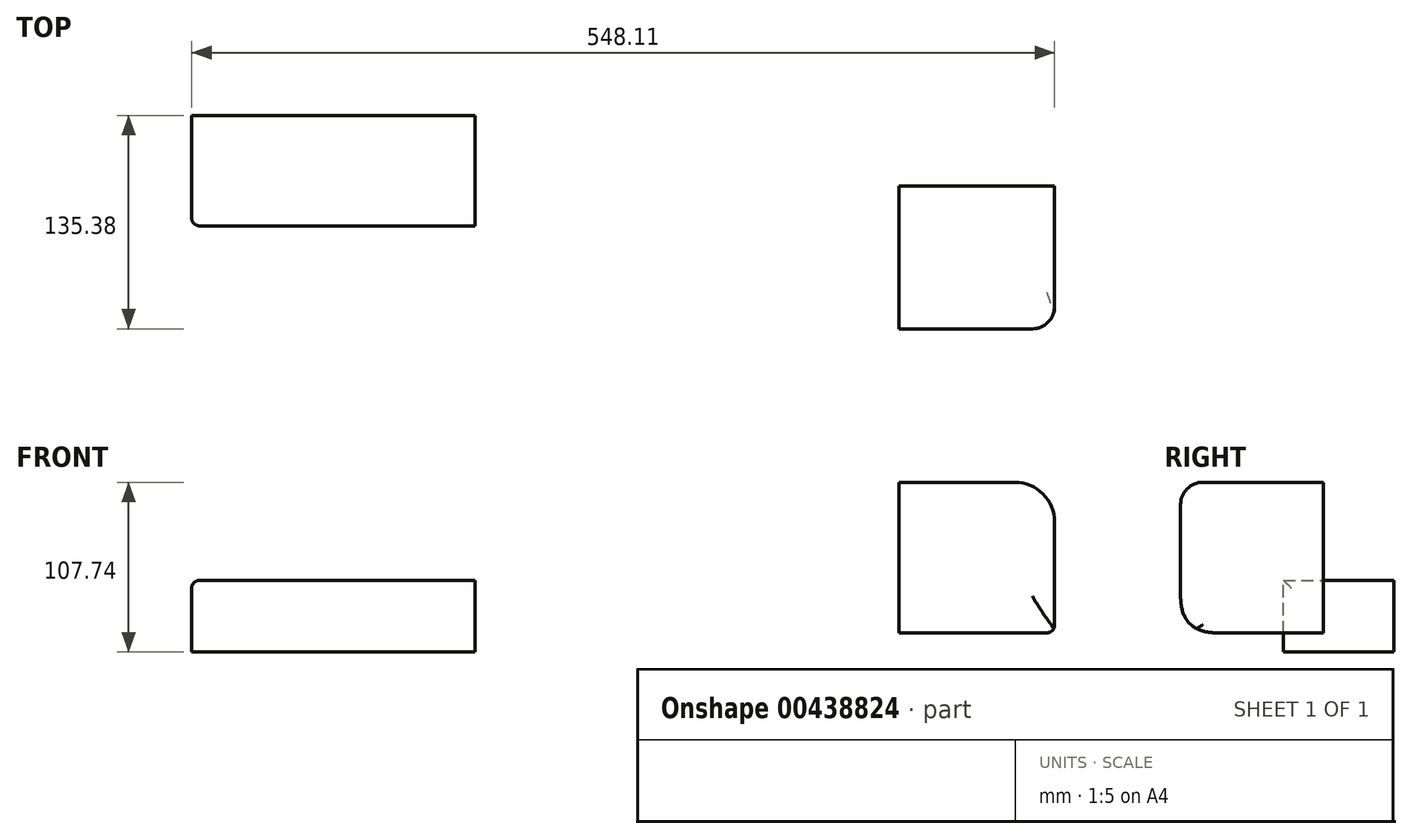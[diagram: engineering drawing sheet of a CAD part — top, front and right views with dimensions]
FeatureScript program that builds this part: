
annotation { "Feature Type Name" : "Feature", "Feature Type Description" : "" }
export const myFeature = defineFeature(function(context is Context, id is Id, definition is map)
    precondition{}
    {
        {
            var Q0;
            Q0=qCreatedBy(makeId("Right.planeOp"),FACE);
            var sketch = newSketch(context, id + "F0", { "sketchPlane" : qUnion([Q0])});
            skLineSegment(sketch, "E0.bottom", {"start": v(-44.5, 62.27) * mm, "end": v(46.04, 62.27) * mm});
            skLineSegment(sketch, "E0.top", {"start": v(-44.5, -33.38) * mm, "end": v(46.04, -33.38) * mm});
            skLineSegment(sketch, "E0.left", {"start": v(-44.5, 62.27) * mm, "end": v(-44.5, -33.38) * mm});
            skLineSegment(sketch, "E0.right", {"start": v(46.04, 62.27) * mm, "end": v(46.04, -33.38) * mm});
            skSolve(sketch);
        }
        {
            var Q0;
            Q0=makeQuery(id+"F0.imprint","IMPRINT",FACE,{"disambiguationData":[TD([[makeQuery(id+"F0.imprint","IMPRINT",EDGE,{"derivedFrom":sQuery(id+"F0.wireOp",EDGE,"E0.bottom")}),-1.0]])]});
            extrude(context, id + "F1", {"entities" : qUnion([Q0]), "depth" : 98.8 * mm});
        }
        {
            var Q0;
            Q0=makeQuery(id+"F1.opExtrude","CAP_EDGE",EDGE,{"disambiguationData":[OSD([sQuery(id+"F0.wireOp",EDGE,"E0.bottom")])],"isStart":false});
            fillet(context, id + "F2", {"entities" : qUnion([Q0]), "radius" : 25.4 * mm, "tangentPropagation" : true, "allowEdgeOverflow" : false});
        }
        {
            var Q0;
            Q0=makeQuery(id+"F1.opExtrude","SWEPT_EDGE",EDGE,{"disambiguationData":[OSD([sQuery(id+"F0.wireOp",EDGE,"E0.bottom"),sQuery(id+"F0.wireOp",EDGE,"E0.left")])]});
            fillet(context, id + "F3", {"entities" : qUnion([Q0]), "radius" : 14.1 * mm, "tangentPropagation" : true, "allowEdgeOverflow" : false});
        }
        {
            var Q0;
            Q0=makeQuery(id+"F1.opExtrude","SWEPT_EDGE",EDGE,{"disambiguationData":[OSD([sQuery(id+"F0.wireOp",EDGE,"E0.top"),sQuery(id+"F0.wireOp",EDGE,"E0.left")])]});
            fillet(context, id + "F4", {"entities" : qUnion([Q0]), "radius" : 23.3 * mm, "rho" : 0.5, "crossSection" : FilletCrossSection.CONIC, "allowEdgeOverflow" : false});
        }
        {
            var Q0;
            Q0=makeQuery(id+"F1.opExtrude","CAP_EDGE",EDGE,{"disambiguationData":[OSD([sQuery(id+"F0.wireOp",EDGE,"E0.top")])],"isStart":false});
            fillet(context, id + "F5", {"entities" : qUnion([Q0]), "radius" : 5.08 * mm, "allowEdgeOverflow" : false});
        }
        {
            var Q0;
            Q0=qCreatedBy(makeId("Top.planeOp"),FACE);
            var sketch = newSketch(context, id + "F6", { "sketchPlane" : qUnion([Q0])});
            skLineSegment(sketch, "E1.bottom", {"start": v(-449.3, 20.85) * mm, "end": v(-269.23, 20.85) * mm});
            skLineSegment(sketch, "E1.top", {"start": v(-449.3, 90.89) * mm, "end": v(-269.23, 90.89) * mm});
            skLineSegment(sketch, "E1.left", {"start": v(-449.3, 20.85) * mm, "end": v(-449.3, 90.89) * mm});
            skLineSegment(sketch, "E1.right", {"start": v(-269.23, 20.85) * mm, "end": v(-269.23, 90.89) * mm});
            skSolve(sketch);
        }
        {
            var Q0;
            Q0=makeQuery(id+"F6.imprint","IMPRINT",FACE,{"disambiguationData":[TD([[makeQuery(id+"F6.imprint","IMPRINT",EDGE,{"derivedFrom":sQuery(id+"F6.wireOp",EDGE,"E1.bottom")}),1.0]])]});
            extrude(context, id + "F7", {"entities" : qUnion([Q0]), "oppositeDirection" : true, "depth" : 45.47 * mm});
        }
        {
            var Q0;
            Q0=makeQuery(id+"F7.opExtrude","CAP_EDGE",EDGE,{"disambiguationData":[OSD([sQuery(id+"F6.wireOp",EDGE,"E1.left")])],"isStart":true});
            var Q1;
            Q1=makeQuery(id+"F7.opExtrude","SWEPT_EDGE",EDGE,{"disambiguationData":[OSD([sQuery(id+"F6.wireOp",EDGE,"E1.bottom"),sQuery(id+"F6.wireOp",EDGE,"E1.left")])]});
            fillet(context, id + "F8", {"entities" : qUnion([Q0, Q1]), "radius" : 5.08 * mm, "tangentPropagation" : true, "allowEdgeOverflow" : false});
        }
    });
